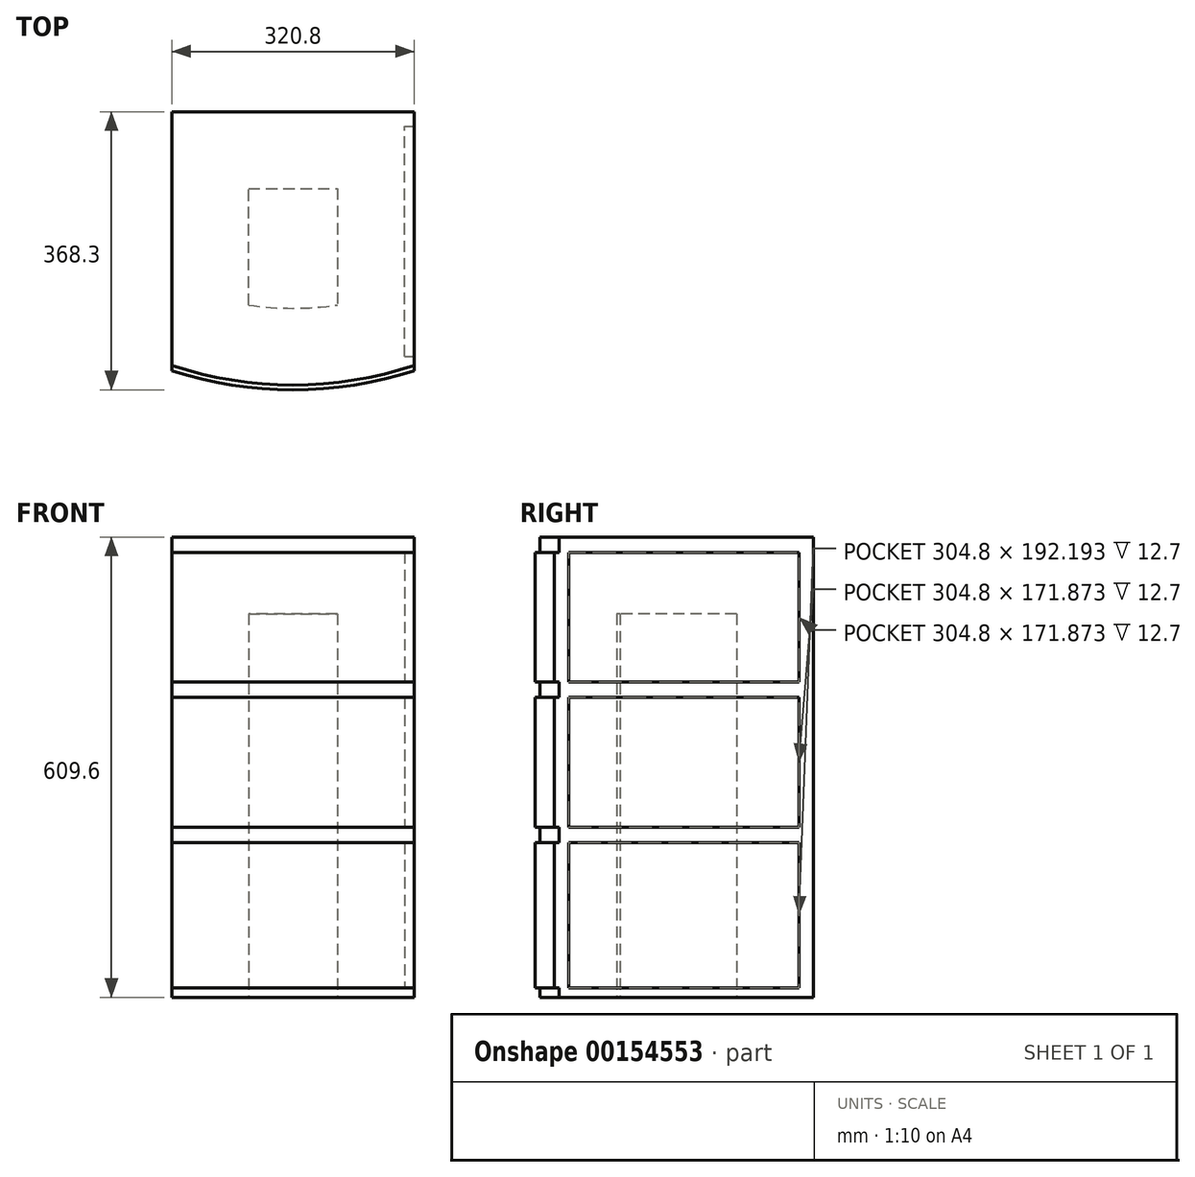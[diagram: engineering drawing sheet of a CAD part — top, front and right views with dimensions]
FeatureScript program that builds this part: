
annotation { "Feature Type Name" : "Feature", "Feature Type Description" : "" }
export const myFeature = defineFeature(function(context is Context, id is Id, definition is map)
    precondition{}
    {
        {
            var Q0;
            Q0=qCreatedBy(makeId("Front.planeOp"),FACE);
            var sketch = newSketch(context, id + "F0", { "sketchPlane" : qUnion([Q0])});
            skLineSegment(sketch, "E0.bottom", {"start": v(0, 0) * mm, "end": v(320.8, 0) * mm});
            skLineSegment(sketch, "E0.top", {"start": v(0, 609.6) * mm, "end": v(320.8, 609.6) * mm});
            skLineSegment(sketch, "E0.left", {"start": v(0, 0) * mm, "end": v(0, 609.6) * mm});
            skLineSegment(sketch, "E0.right", {"start": v(320.8, 0) * mm, "end": v(320.8, 609.6) * mm});
            skSolve(sketch);
        }
        {
            var Q0;
            Q0=makeQuery(id+"F0.imprint","IMPRINT",FACE,{"disambiguationData":[TD([[makeQuery(id+"F0.imprint","IMPRINT",EDGE,{"derivedFrom":sQuery(id+"F0.wireOp",EDGE,"E0.bottom")}),1.0]])]});
            extrude(context, id + "F1", {"entities" : qUnion([Q0]), "oppositeDirection" : true, "depth" : 368.3 * mm});
        }
        {
            var Q0;
            Q0=makeQuery(id+"F1.opExtrude","SWEPT_FACE",FACE,{"disambiguationData":[OSD([sQuery(id+"F0.wireOp",EDGE,"E0.top")])]});
            var sketch = newSketch(context, id + "F2", { "sketchPlane" : qUnion([Q0])});
            skCircle(sketch, "E1", {"center": v(160.4, 519.17) * mm, "radius": 519.17 * mm});
            skPoint(sketch, "E1.first.point", {"position": v(0, 25.4) * mm});
            skPoint(sketch, "E1.second.point", {"position": v(320.8, 25.4) * mm});
            skPoint(sketch, "E1.third.point", {"position": v(160.4, 0) * mm});
            skLineSegment(sketch, "E2", {"start": v(160.4, 519.17) * mm, "end": v(160.4, 0) * mm, "construction": true});
            skLineSegment(sketch, "E3", {"start": v(0, 25.4) * mm, "end": v(0, 0) * mm});
            skLineSegment(sketch, "E4", {"start": v(0, 0) * mm, "end": v(320.8, 0) * mm});
            skLineSegment(sketch, "E5", {"start": v(320.8, 0) * mm, "end": v(320.8, 25.4) * mm});
            skSolve(sketch);
        }
        {
            var Q0;
            {var subQ0=sQuery(id+"F2.wireOp",EDGE,"E3");Q0=makeQuery(id+"F2.imprint","IMPRINT",FACE,{"disambiguationData":[TD([[makeQuery(id+"F2.imprint","IMPRINT",EDGE,{"derivedFrom":subQ0}),1.0]])]});}
            var Q1;
            {var subQ0=sQuery(id+"F2.wireOp",EDGE,"E5");Q1=makeQuery(id+"F2.imprint","IMPRINT",FACE,{"disambiguationData":[TD([[makeQuery(id+"F2.imprint","IMPRINT",EDGE,{"derivedFrom":subQ0}),-1.0]])]});}
            extrude(context, id + "F3", {"entities" : qUnion([Q0, Q1]), "operationType" : NewBodyOperationType.REMOVE, "endBound" : BoundingType.THROUGH_ALL, "oppositeDirection" : true, "depth" : 30.48 * mm});
        }
        {
            var Q0;
            Q0=qCreatedBy(makeId("Front.planeOp"),FACE);
            var sketch = newSketch(context, id + "F4", { "sketchPlane" : qUnion([Q0])});
            skLineSegment(sketch, "E6.0", {"start": v(0, 609.6) * mm, "end": v(320.8, 609.6) * mm});
            skLineSegment(sketch, "E6.1", {"start": v(320.8, 0) * mm, "end": v(0, 0) * mm});
            skLineSegment(sketch, "E6.2", {"start": v(320.8, 0) * mm, "end": v(320.8, 609.6) * mm});
            skLineSegment(sketch, "E6.3", {"start": v(0, 0) * mm, "end": v(0, 609.6) * mm});
            skLineSegment(sketch, "E7", {"start": v(0, 589.28) * mm, "end": v(320.8, 589.28) * mm});
            skLineSegment(sketch, "E8", {"start": v(320.8, 397.09) * mm, "end": v(0, 397.09) * mm});
            skLineSegment(sketch, "E9", {"start": v(0, 225.21) * mm, "end": v(320.8, 225.21) * mm});
            skLineSegment(sketch, "E10", {"start": v(0, 417.4) * mm, "end": v(320.8, 417.4) * mm});
            skLineSegment(sketch, "E11", {"start": v(0, 204.9) * mm, "end": v(320.8, 204.9) * mm});
            skLineSegment(sketch, "E12", {"start": v(0, 12.7) * mm, "end": v(320.8, 12.7) * mm});
            skLineSegment(sketch, "E13", {"start": v(160.4, 609.6) * mm, "end": v(160.4, 589.28) * mm, "construction": true});
            skLineSegment(sketch, "E14", {"start": v(160.4, 589.28) * mm, "end": v(160.4, 397.09) * mm, "construction": true});
            skLineSegment(sketch, "E15", {"start": v(160.4, 417.4) * mm, "end": v(160.4, 397.09) * mm, "construction": true});
            skLineSegment(sketch, "E16", {"start": v(160.4, 417.4) * mm, "end": v(160.4, 225.21) * mm, "construction": true});
            skLineSegment(sketch, "E17", {"start": v(160.4, 225.21) * mm, "end": v(160.4, 204.9) * mm, "construction": true});
            skLineSegment(sketch, "E18", {"start": v(160.4, 204.9) * mm, "end": v(160.4, 12.7) * mm, "construction": true});
            skSolve(sketch);
        }
        {
            var Q0;
            Q0=makeQuery(id+"F1.opExtrude","SWEPT_FACE",FACE,{"disambiguationData":[OSD([sQuery(id+"F0.wireOp",EDGE,"E0.right")])]});
            var Q1;
            Q1=makeQuery(id+"F1.opExtrude","SWEPT_FACE",FACE,{"disambiguationData":[OSD([sQuery(id+"F0.wireOp",EDGE,"E0.left")])]});
            cPlane(context, id + "F5", {"entities" : qUnion([Q0, Q1]), "cplaneType" : CPlaneType.MID_PLANE, "offset" : 25.4 * mm, "width" : 152.4 * mm, "height" : 152.4 * mm});
        }
        {
            var Q0;
            Q0=qCreatedBy(id+"F5.planeOp",FACE);
            var sketch = newSketch(context, id + "F6", { "sketchPlane" : qUnion([Q0])});
            skLineSegment(sketch, "E19.0", {"start": v(0, 609.6) * mm, "end": v(0, 589.28) * mm});
            skLineSegment(sketch, "E19.1", {"start": v(0, 417.4) * mm, "end": v(0, 397.09) * mm});
            skLineSegment(sketch, "E19.2", {"start": v(0, 225.21) * mm, "end": v(0, 204.9) * mm});
            skLineSegment(sketch, "E20", {"start": v(0, 609.6) * mm, "end": v(6.35, 609.6) * mm});
            skLineSegment(sketch, "E21", {"start": v(6.35, 609.6) * mm, "end": v(6.35, 589.28) * mm});
            skLineSegment(sketch, "E22", {"start": v(6.35, 589.28) * mm, "end": v(0, 589.28) * mm});
            skLineSegment(sketch, "E23", {"start": v(0, 417.4) * mm, "end": v(6.35, 417.4) * mm});
            skLineSegment(sketch, "E24", {"start": v(6.35, 417.4) * mm, "end": v(6.35, 397.09) * mm});
            skLineSegment(sketch, "E25", {"start": v(6.35, 397.09) * mm, "end": v(0, 397.09) * mm});
            skLineSegment(sketch, "E26", {"start": v(0, 204.9) * mm, "end": v(6.35, 204.9) * mm});
            skLineSegment(sketch, "E27", {"start": v(6.35, 204.9) * mm, "end": v(6.35, 225.21) * mm});
            skLineSegment(sketch, "E28", {"start": v(6.35, 225.21) * mm, "end": v(0, 225.21) * mm});
            skLineSegment(sketch, "E29", {"start": v(519.17, 609.6) * mm, "end": v(519.17, 467.62) * mm});
            skLineSegment(sketch, "E30.bottom", {"start": v(0, 0) * mm, "end": v(6.35, 0) * mm});
            skLineSegment(sketch, "E30.top", {"start": v(0, 12.7) * mm, "end": v(6.35, 12.7) * mm});
            skLineSegment(sketch, "E30.left", {"start": v(0, 0) * mm, "end": v(0, 12.7) * mm});
            skLineSegment(sketch, "E30.right", {"start": v(6.35, 0) * mm, "end": v(6.35, 12.7) * mm});
            skSolve(sketch);
        }
        {
            var Q0;
            Q0=makeQuery(id+"F6.imprint","IMPRINT",FACE,{"disambiguationData":[TD([[makeQuery(id+"F6.imprint","IMPRINT",EDGE,{"derivedFrom":sQuery(id+"F6.wireOp",EDGE,"E19.0")}),1.0]])]});
            var Q1;
            Q1=makeQuery(id+"F6.imprint","IMPRINT",FACE,{"disambiguationData":[TD([[makeQuery(id+"F6.imprint","IMPRINT",EDGE,{"derivedFrom":sQuery(id+"F6.wireOp",EDGE,"E19.1")}),1.0]])]});
            var Q2;
            Q2=makeQuery(id+"F6.imprint","IMPRINT",FACE,{"disambiguationData":[TD([[makeQuery(id+"F6.imprint","IMPRINT",EDGE,{"derivedFrom":sQuery(id+"F6.wireOp",EDGE,"E19.2")}),1.0]])]});
            var Q3;
            Q3=makeQuery(id+"F6.imprint","IMPRINT",FACE,{"disambiguationData":[TD([[makeQuery(id+"F6.imprint","IMPRINT",EDGE,{"derivedFrom":sQuery(id+"F6.wireOp",EDGE,"E30.bottom")}),1.0]])]});
            var Q4;
            Q4=sQuery(id+"F6.wireOp",EDGE,"E29");
            revolve(context, id + "F7", {"operationType" : NewBodyOperationType.REMOVE, "entities" : qUnion([Q0, Q1, Q2, Q3]), "axis" : qUnion([Q4]), "revolveType" : RevolveType.FULL, "oppositeDirection" : true});
        }
        {
            var Q0;
            Q0=makeQuery(id+"F1.opExtrude","SWEPT_FACE",FACE,{"disambiguationData":[OSD([sQuery(id+"F0.wireOp",EDGE,"E0.right")])]});
            var sketch = newSketch(context, id + "F8", { "sketchPlane" : qUnion([Q0])});
            skLineSegment(sketch, "E31.bottom", {"start": v(349.25, 589.28) * mm, "end": v(44.45, 589.28) * mm});
            skLineSegment(sketch, "E31.top", {"start": v(349.25, 417.4) * mm, "end": v(44.45, 417.4) * mm});
            skLineSegment(sketch, "E31.right", {"start": v(44.45, 589.28) * mm, "end": v(44.45, 417.4) * mm});
            skLineSegment(sketch, "E32.bottom", {"start": v(349.25, 397.09) * mm, "end": v(44.45, 397.09) * mm});
            skLineSegment(sketch, "E32.top", {"start": v(349.25, 225.21) * mm, "end": v(44.45, 225.21) * mm});
            skLineSegment(sketch, "E32.right", {"start": v(44.45, 397.09) * mm, "end": v(44.45, 225.21) * mm});
            skLineSegment(sketch, "E33.bottom", {"start": v(44.45, 204.9) * mm, "end": v(349.25, 204.9) * mm});
            skLineSegment(sketch, "E33.top", {"start": v(44.45, 12.7) * mm, "end": v(349.25, 12.7) * mm});
            skLineSegment(sketch, "E33.left", {"start": v(44.45, 204.9) * mm, "end": v(44.45, 12.7) * mm});
            skLineSegment(sketch, "E34", {"start": v(349.25, 589.28) * mm, "end": v(349.25, 417.4) * mm});
            skLineSegment(sketch, "E35", {"start": v(349.25, 397.09) * mm, "end": v(349.25, 225.21) * mm});
            skLineSegment(sketch, "E36", {"start": v(349.25, 204.9) * mm, "end": v(349.25, 12.7) * mm});
            skPoint(sketch, "E31.left.start.orphan", {"position": v(368.3, 589.28) * mm});
            skSolve(sketch);
        }
        {
            var Q0;
            Q0=makeQuery(id+"F8.imprint","IMPRINT",FACE,{"disambiguationData":[TD([[makeQuery(id+"F8.imprint","IMPRINT",EDGE,{"derivedFrom":sQuery(id+"F8.wireOp",EDGE,"E31.bottom")}),1.0]])]});
            var Q1;
            Q1=makeQuery(id+"F8.imprint","IMPRINT",FACE,{"disambiguationData":[TD([[makeQuery(id+"F8.imprint","IMPRINT",EDGE,{"derivedFrom":sQuery(id+"F8.wireOp",EDGE,"E32.bottom")}),1.0]])]});
            var Q2;
            Q2=makeQuery(id+"F8.imprint","IMPRINT",FACE,{"disambiguationData":[TD([[makeQuery(id+"F8.imprint","IMPRINT",EDGE,{"derivedFrom":sQuery(id+"F8.wireOp",EDGE,"E33.bottom")}),-1.0]])]});
            extrude(context, id + "F9", {"entities" : qUnion([Q0, Q1, Q2]), "operationType" : NewBodyOperationType.REMOVE, "oppositeDirection" : true, "depth" : 12.7 * mm});
        }
        {
            var Q0;
            Q0=makeQuery(id+"F1.opExtrude","SWEPT_FACE",FACE,{"disambiguationData":[OSD([sQuery(id+"F0.wireOp",EDGE,"E0.bottom")])]});
            var sketch = newSketch(context, id + "F10", { "sketchPlane" : qUnion([Q0])});
            skLineSegment(sketch, "E37.0", {"start": v(219.2, -266.7) * mm, "end": v(219.2, -112.18) * mm});
            skLineSegment(sketch, "E37.1", {"start": v(101.6, -266.7) * mm, "end": v(219.2, -266.7) * mm});
            skLineSegment(sketch, "E37.2", {"start": v(101.6, -112.18) * mm, "end": v(101.6, -266.7) * mm});
            skArc(sketch, "E37.3", {"start": v(219.2, -112.18) * mm, "mid": v(160.4, -107.95) * mm, "end": v(101.6, -112.18) * mm});
            skSolve(sketch);
        }
        {
            var Q0;
            Q0 = qSketchRegion(id + "F10", true);
            extrude(context, id + "F11", {"entities" : qUnion([Q0]), "operationType" : NewBodyOperationType.REMOVE, "oppositeDirection" : true, "depth" : 508 * mm});
        }
    });
